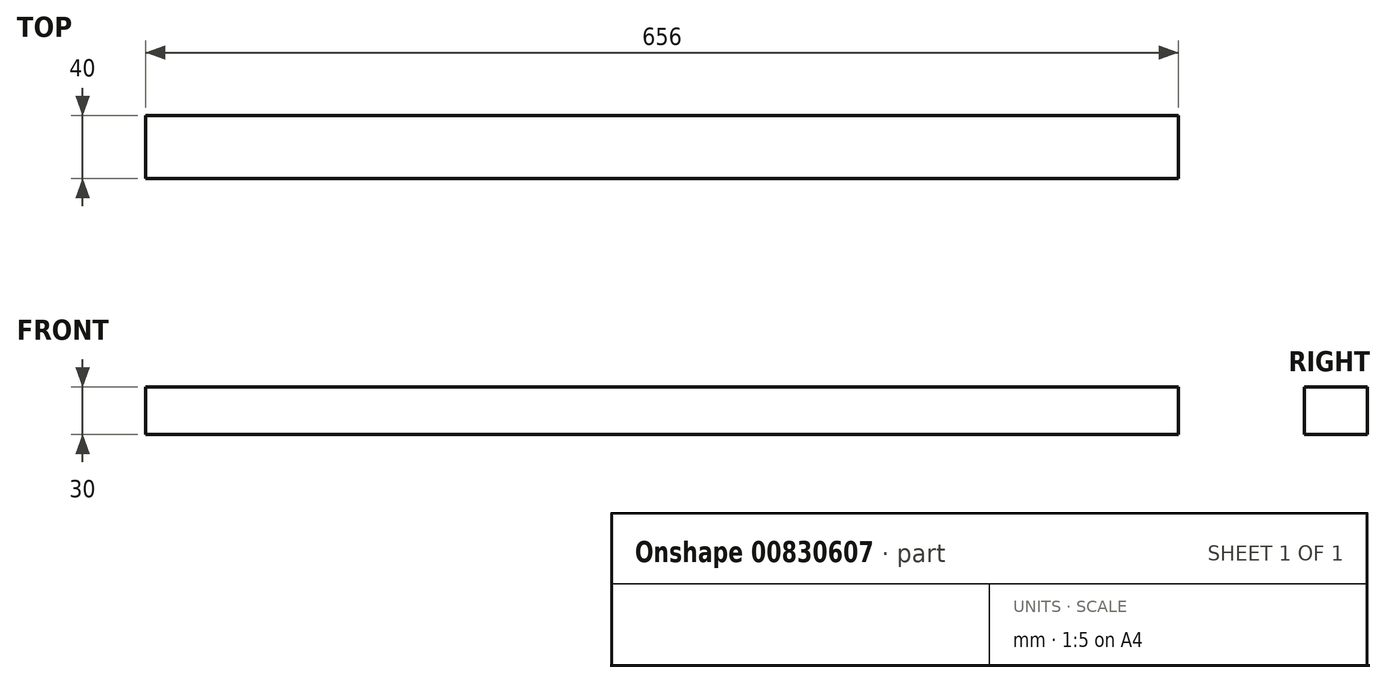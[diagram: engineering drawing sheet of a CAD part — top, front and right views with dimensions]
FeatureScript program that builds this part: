
annotation { "Feature Type Name" : "Feature", "Feature Type Description" : "" }
export const myFeature = defineFeature(function(context is Context, id is Id, definition is map)
    precondition{}
    {
        {
            var Q0;
            Q0=qCreatedBy(makeId("Right.planeOp"),FACE);
            var sketch = newSketch(context, id + "F0", { "sketchPlane" : qUnion([Q0])});
            skLineSegment(sketch, "E0.bottom", {"start": v(0, 0) * mm, "end": v(40, 0) * mm});
            skLineSegment(sketch, "E0.top", {"start": v(0, 30) * mm, "end": v(40, 30) * mm});
            skLineSegment(sketch, "E0.left", {"start": v(0, 0) * mm, "end": v(0, 30) * mm});
            skLineSegment(sketch, "E0.right", {"start": v(40, 0) * mm, "end": v(40, 30) * mm});
            skSolve(sketch);
        }
        {
            var Q0;
            Q0=makeQuery(id+"F0.imprint","IMPRINT",FACE,{"disambiguationData":[TD([[makeQuery(id+"F0.imprint","IMPRINT",EDGE,{"derivedFrom":sQuery(id+"F0.wireOp",EDGE,"E0.bottom")}),1.0]])]});
            extrude(context, id + "F1", {"entities" : qUnion([Q0]), "depth" : 656 * mm, "offsetDistance" : 25 * mm});
        }
    });
